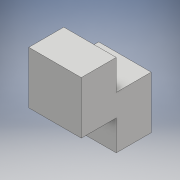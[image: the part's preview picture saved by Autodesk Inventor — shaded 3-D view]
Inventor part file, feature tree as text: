
AUTODESK INVENTOR PART (.ipt)
format: ipt  version: 2017 (Build 210142000, 142)  size: 99,328 bytes
history: native  units: mm
features: extrude x2, sketch x2
ambient origin geometry x8: Origin, YZ Plane, XZ Plane, XY Plane, X Axis, Y Axis, Z Axis, Center Point
bodies: Solide1 (feature_tree)
feature tree (4):
  extrude  "Extrusion1"  Depth=15.0mm
  extrude  "Extrusion2"  Depth=15.0mm
  sketch  "Esquisse1"
  sketch  "Esquisse2"
